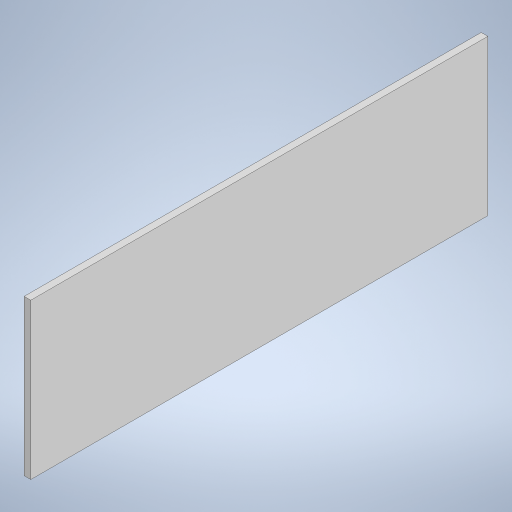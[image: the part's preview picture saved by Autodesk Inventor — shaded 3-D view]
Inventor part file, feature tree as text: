
AUTODESK INVENTOR PART (.ipt)
format: ipt  version: 2024.3 (Build 283343000, 343)  size: 187,904 bytes
history: native  units: mm
features: extrude x1, sketch x1
ambient origin geometry x8: Origin, YZ Plane, XZ Plane, XY Plane, X Axis, Y Axis, Z Axis, Center Point
bodies: Solid1 (feature_tree)
feature tree (2):
  extrude  "Extrusion1"  Depth=206.0mm
  sketch  "Sketch1"  dims[d0=70.0mm d1=206.0mm d2=3.0mm d3=0.0mm]
